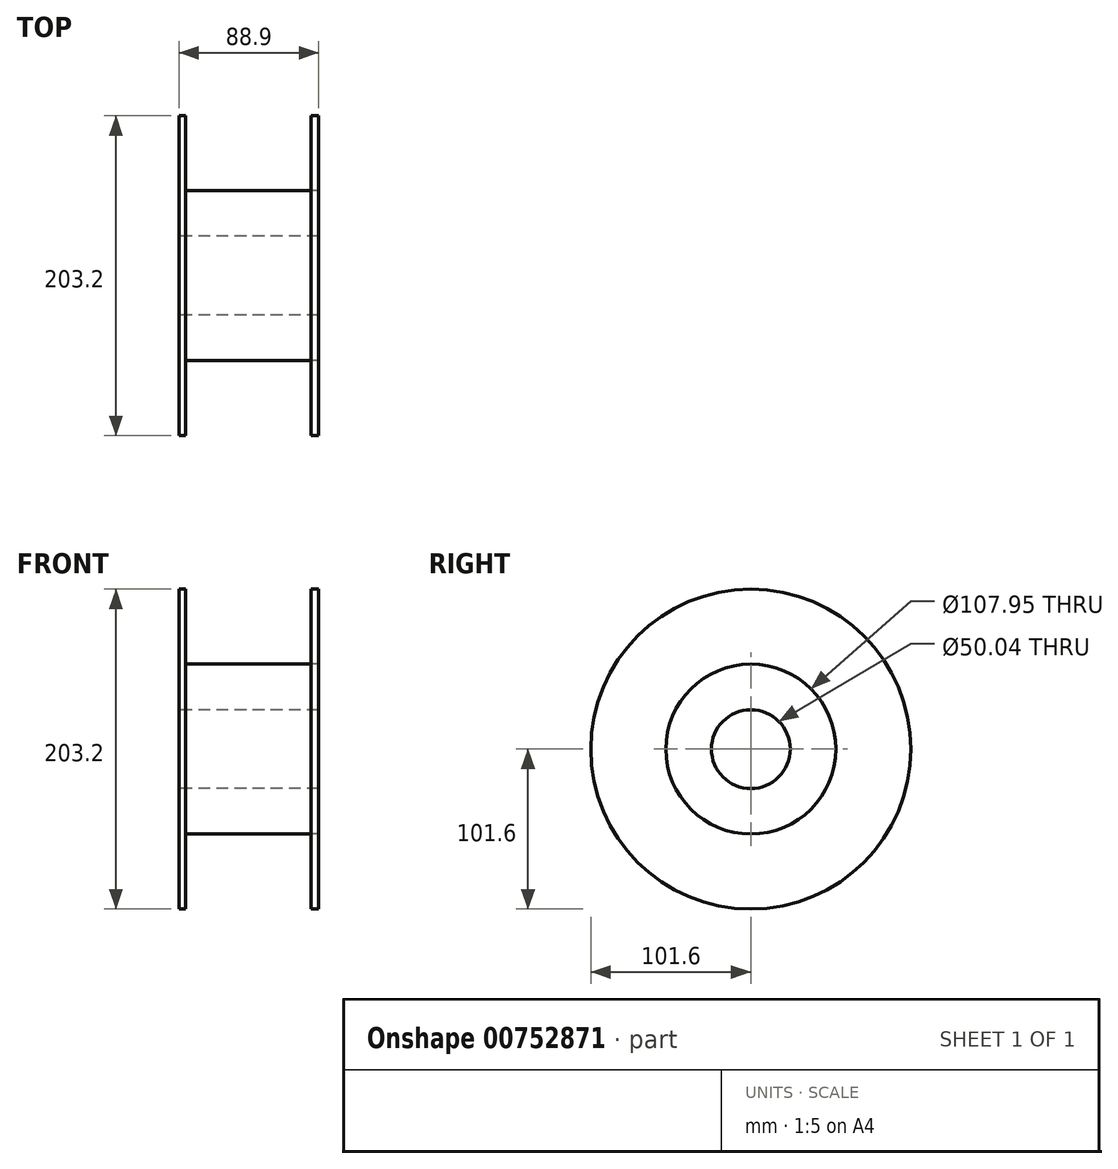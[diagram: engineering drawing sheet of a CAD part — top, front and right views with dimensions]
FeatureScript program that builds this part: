
annotation { "Feature Type Name" : "Feature", "Feature Type Description" : "" }
export const myFeature = defineFeature(function(context is Context, id is Id, definition is map)
    precondition{}
    {
        {
            var Q0;
            Q0=qCreatedBy(makeId("Right.planeOp"),FACE);
            var sketch = newSketch(context, id + "F0", { "sketchPlane" : qUnion([Q0])});
            skCircle(sketch, "E0", {"center": v(0, 0) * mm, "radius": 25.02 * mm});
            skCircle(sketch, "E1", {"center": v(0, 0) * mm, "radius": 53.98 * mm});
            skCircle(sketch, "E2", {"center": v(0, 0) * mm, "radius": 101.6 * mm});
            skSolve(sketch);
        }
        {
            var Q0;
            Q0=makeQuery(id+"F0.imprint","IMPRINT",FACE,{"disambiguationData":[TD([[makeQuery(id+"F0.imprint","IMPRINT",EDGE,{"derivedFrom":sQuery(id+"F0.wireOp",EDGE,"E1")}),-1.0]])]});
            var Q1;
            Q1=makeQuery(id+"F0.imprint","IMPRINT",FACE,{"disambiguationData":[TD([[makeQuery(id+"F0.imprint","IMPRINT",EDGE,{"derivedFrom":sQuery(id+"F0.wireOp",EDGE,"E0")}),-1.0]])]});
            extrude(context, id + "F1", {"entities" : qUnion([Q0, Q1]), "depth" : 4.32 * mm, "offsetDistance" : 25.4 * mm});
        }
        {
            var Q0;
            Q0=makeQuery(id+"F0.imprint","IMPRINT",FACE,{"disambiguationData":[TD([[makeQuery(id+"F0.imprint","IMPRINT",EDGE,{"derivedFrom":sQuery(id+"F0.wireOp",EDGE,"E0")}),-1.0]])]});
            extrude(context, id + "F2", {"entities" : qUnion([Q0]), "operationType" : NewBodyOperationType.ADD, "depth" : 88.9 * mm, "offsetDistance" : 25.4 * mm});
        }
        {
            var Q0;
            Q0=makeQuery(id+"F0.imprint","IMPRINT",FACE,{"disambiguationData":[TD([[makeQuery(id+"F0.imprint","IMPRINT",EDGE,{"derivedFrom":sQuery(id+"F0.wireOp",EDGE,"E1")}),-1.0]])]});
            extrude(context, id + "F3", {"entities" : qUnion([Q0]), "depth" : 88.9 * mm, "offsetDistance" : 25.4 * mm, "hasSecondDirection" : true, "secondDirectionOppositeDirection" : false, "secondDirectionDepth" : 84.07 * mm});
        }
    });
